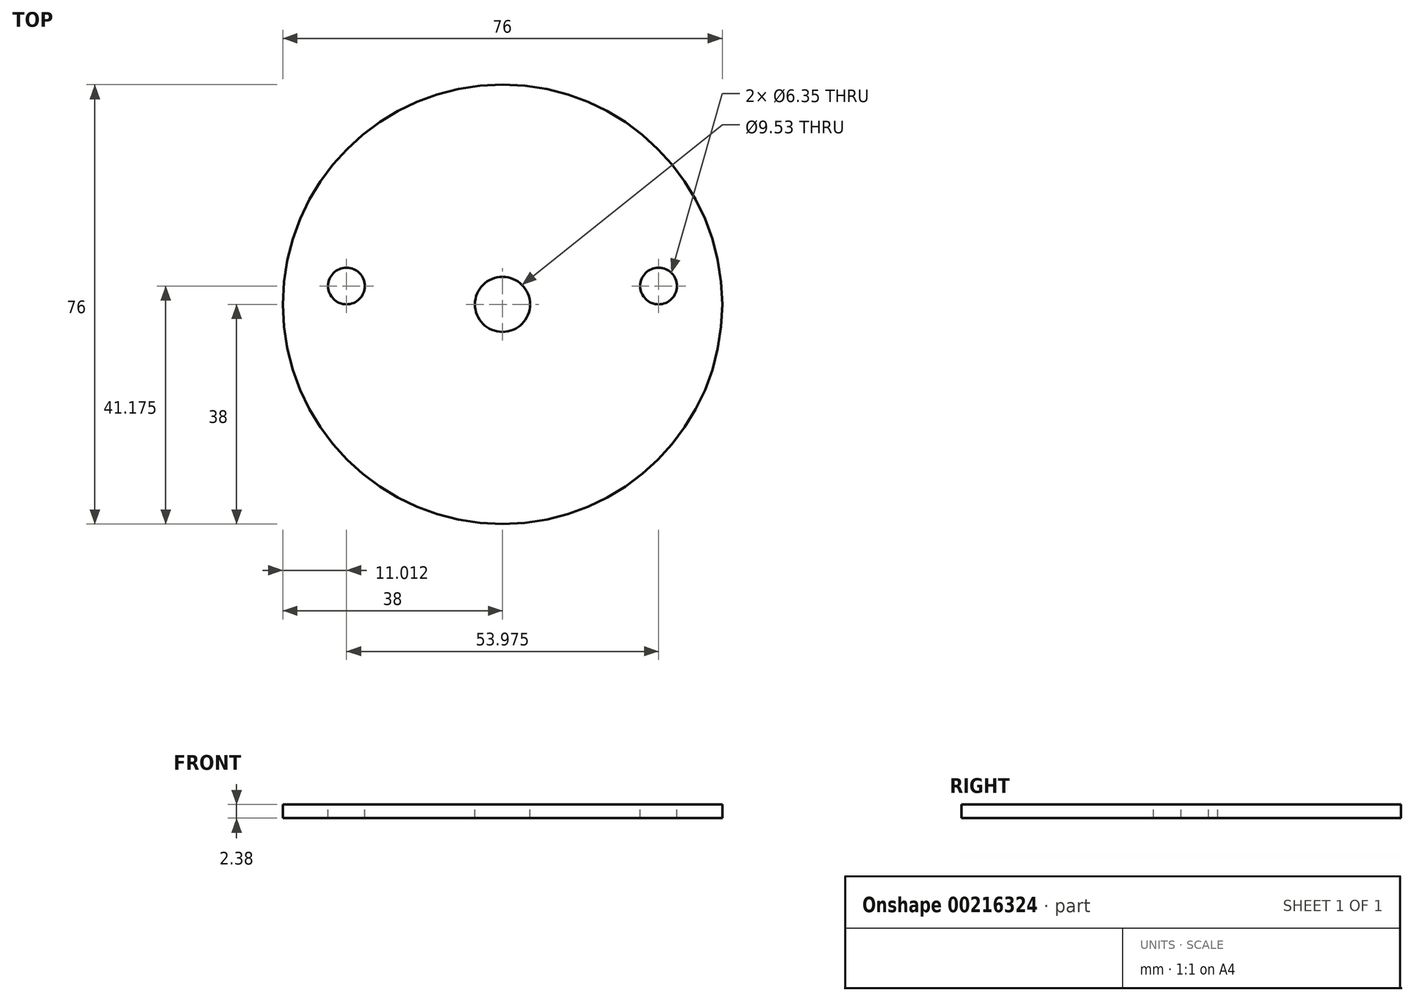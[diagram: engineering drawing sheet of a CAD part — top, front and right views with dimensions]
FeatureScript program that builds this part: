
annotation { "Feature Type Name" : "Feature", "Feature Type Description" : "" }
export const myFeature = defineFeature(function(context is Context, id is Id, definition is map)
    precondition{}
    {
        {
            var Q0;
            Q0=qCreatedBy(makeId("Top.planeOp"),FACE);
            var sketch = newSketch(context, id + "F0", { "sketchPlane" : qUnion([Q0])});
            skCircle(sketch, "E0", {"center": v(0, 0) * mm, "radius": 38 * mm});
            skSolve(sketch);
        }
        {
            var Q0;
            Q0 = qSketchRegion(id + "F0", true);
            extrude(context, id + "F1", {"entities" : qUnion([Q0]), "depth" : 2.38 * mm});
        }
        {
            var Q0;
            Q0=makeQuery(id+"F1.opExtrude","CAP_FACE",FACE,{"disambiguationData":[OSD([sQuery(id+"F0.wireOp",EDGE,"E0")])],"isStart":false});
            var sketch = newSketch(context, id + "F2", { "sketchPlane" : qUnion([Q0])});
            skCircle(sketch, "E1", {"center": v(0, 0) * mm, "radius": 4.76 * mm});
            skCircle(sketch, "E2", {"center": v(26.99, 3.18) * mm, "radius": 3.18 * mm});
            skCircle(sketch, "E3", {"center": v(-26.99, 3.18) * mm, "radius": 3.18 * mm});
            skSolve(sketch);
        }
        {
            var Q0;
            Q0 = qSketchRegion(id + "F2", true);
            extrude(context, id + "F3", {"entities" : qUnion([Q0]), "operationType" : NewBodyOperationType.REMOVE, "oppositeDirection" : true, "depth" : 25.4 * mm});
        }
    });
